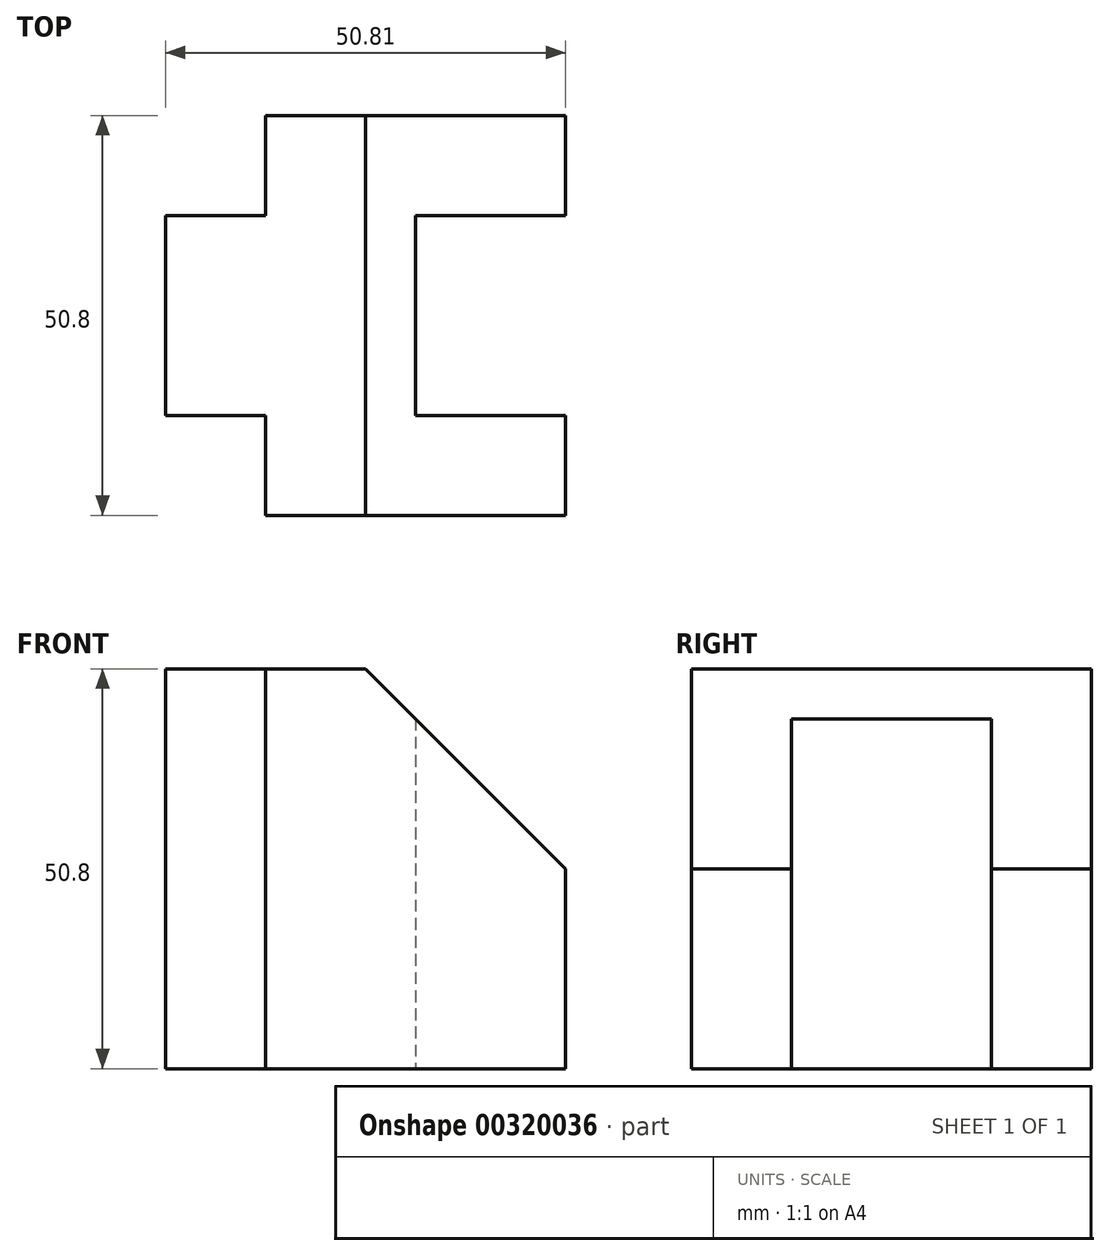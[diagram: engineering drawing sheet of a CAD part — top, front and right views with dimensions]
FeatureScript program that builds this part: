
annotation { "Feature Type Name" : "Feature", "Feature Type Description" : "" }
export const myFeature = defineFeature(function(context is Context, id is Id, definition is map)
    precondition{}
    {
        {
            var Q0;
            Q0=qCreatedBy(makeId("Front.planeOp"),FACE);
            var sketch = newSketch(context, id + "F0", { "sketchPlane" : qUnion([Q0])});
            skLineSegment(sketch, "E0", {"start": v(0, 0) * mm, "end": v(0, 50.8) * mm});
            skLineSegment(sketch, "E1", {"start": v(38.1, 0) * mm, "end": v(0, 0) * mm});
            skLineSegment(sketch, "E2", {"start": v(0, 50.8) * mm, "end": v(12.7, 50.8) * mm});
            skLineSegment(sketch, "E3", {"start": v(12.7, 50.8) * mm, "end": v(38.1, 25.4) * mm});
            skLineSegment(sketch, "E4", {"start": v(38.1, 25.4) * mm, "end": v(38.1, 0) * mm});
            skSolve(sketch);
        }
        {
            var Q0;
            Q0 = qSketchRegion(id + "F0", true);
            extrude(context, id + "F1", {"entities" : qUnion([Q0]), "depth" : 12.7 * mm});
        }
        {
            var Q0;
            Q0=makeQuery(id+"F1.opExtrude","CAP_FACE",FACE,{"disambiguationData":[OSD([sQuery(id+"F0.wireOp",EDGE,"E0"),sQuery(id+"F0.wireOp",EDGE,"E1"),sQuery(id+"F0.wireOp",EDGE,"E2"),sQuery(id+"F0.wireOp",EDGE,"E3"),sQuery(id+"F0.wireOp",EDGE,"E4")])],"isStart":false});
            var sketch = newSketch(context, id + "F2", { "sketchPlane" : qUnion([Q0])});
            skLineSegment(sketch, "E5", {"start": v(0, 0) * mm, "end": v(-12.7, 0) * mm});
            skLineSegment(sketch, "E6", {"start": v(-12.7, 0) * mm, "end": v(-12.7, 50.8) * mm});
            skLineSegment(sketch, "E7", {"start": v(-12.7, 50.8) * mm, "end": v(0, 50.8) * mm});
            skLineSegment(sketch, "E8", {"start": v(0, 50.8) * mm, "end": v(12.7, 50.8) * mm});
            skLineSegment(sketch, "E9", {"start": v(12.7, 50.8) * mm, "end": v(19.05, 44.45) * mm});
            skLineSegment(sketch, "E10", {"start": v(19.05, 44.45) * mm, "end": v(19.05, 0) * mm});
            skLineSegment(sketch, "E11", {"start": v(19.05, 0) * mm, "end": v(0, 0) * mm});
            skSolve(sketch);
        }
        {
            var Q0;
            Q0 = qSketchRegion(id + "F2", true);
            extrude(context, id + "F3", {"entities" : qUnion([Q0]), "operationType" : NewBodyOperationType.ADD, "depth" : 25.4 * mm});
        }
        {
            var Q0;
            Q0=makeQuery(id+"F3.opExtrude","CAP_FACE",FACE,{"disambiguationData":[OSD([sQuery(id+"F2.wireOp",EDGE,"E5"),sQuery(id+"F2.wireOp",EDGE,"E6"),sQuery(id+"F2.wireOp",EDGE,"E7"),sQuery(id+"F2.wireOp",EDGE,"E8"),sQuery(id+"F2.wireOp",EDGE,"E9"),sQuery(id+"F2.wireOp",EDGE,"E10"),sQuery(id+"F2.wireOp",EDGE,"E11")])],"isStart":false});
            var sketch = newSketch(context, id + "F4", { "sketchPlane" : qUnion([Q0])});
            skLineSegment(sketch, "E12", {"start": v(0, 0) * mm, "end": v(0, 50.8) * mm});
            skLineSegment(sketch, "E13", {"start": v(0, 50.8) * mm, "end": v(12.7, 50.8) * mm});
            skLineSegment(sketch, "E14", {"start": v(12.7, 50.8) * mm, "end": v(38.1, 25.4) * mm});
            skLineSegment(sketch, "E15", {"start": v(38.1, 25.4) * mm, "end": v(38.1, 0) * mm});
            skLineSegment(sketch, "E16", {"start": v(38.1, 0) * mm, "end": v(0, 0) * mm});
            skSolve(sketch);
        }
        {
            var Q0;
            Q0 = qSketchRegion(id + "F4", true);
            extrude(context, id + "F5", {"entities" : qUnion([Q0]), "operationType" : NewBodyOperationType.ADD, "depth" : 12.7 * mm});
        }
    });
